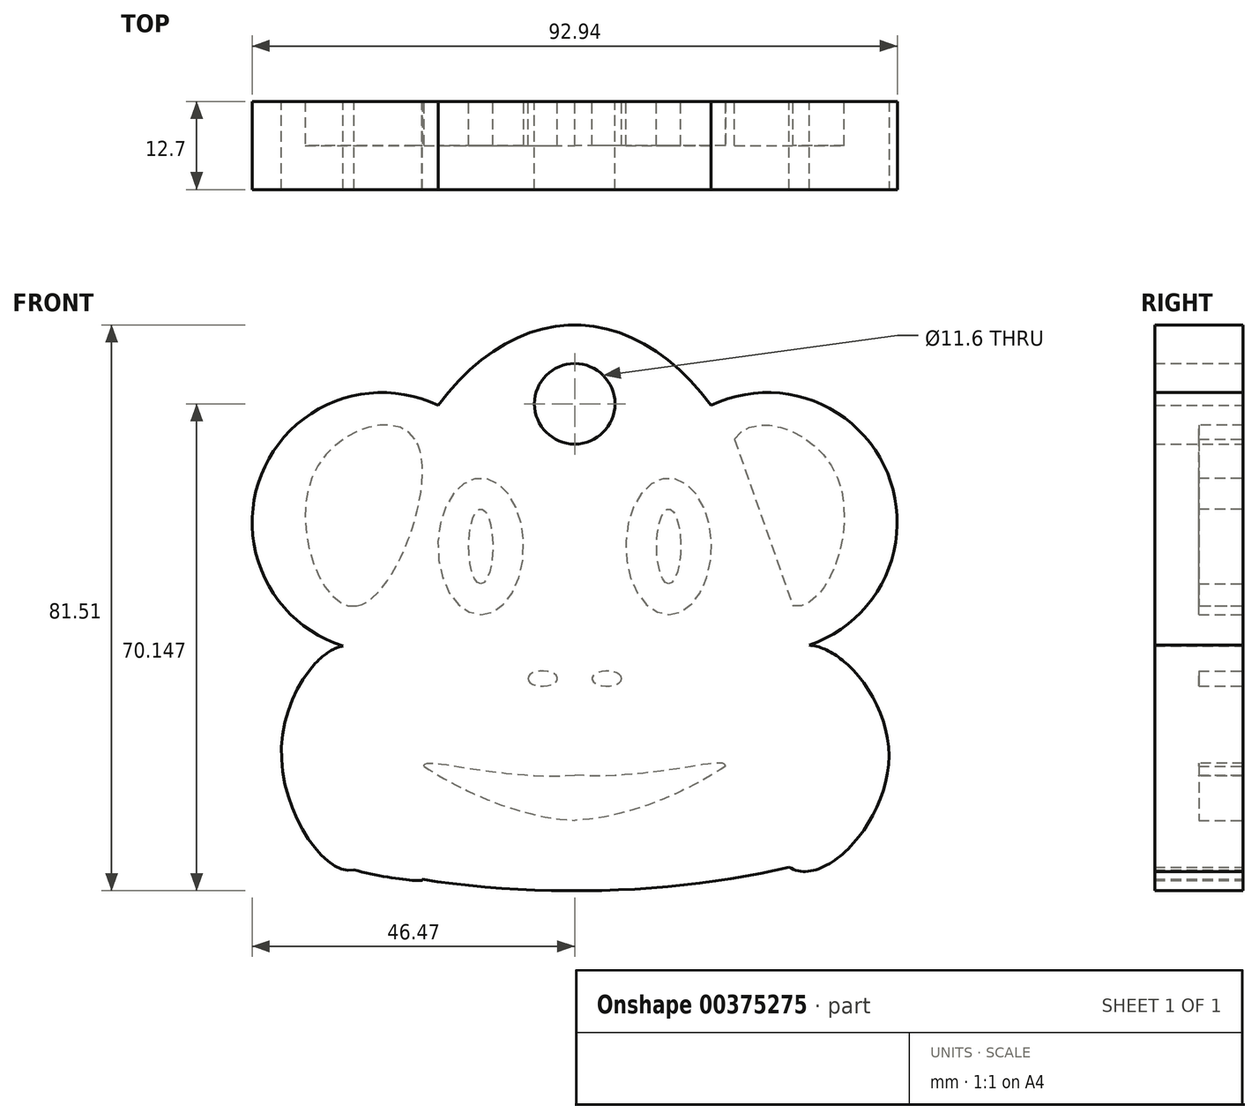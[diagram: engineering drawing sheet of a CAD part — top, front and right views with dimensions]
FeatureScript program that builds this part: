
annotation { "Feature Type Name" : "Feature", "Feature Type Description" : "" }
export const myFeature = defineFeature(function(context is Context, id is Id, definition is map)
    precondition{}
    {
        {
            var Q0;
            Q0=qCreatedBy(makeId("Front.planeOp"),FACE);
            var sketch = newSketch(context, id + "F0", { "sketchPlane" : qUnion([Q0])});
            skEllipticalArc(sketch, "E0", {});
            skEllipticalArc(sketch, "E1.trimOffspring", {});
            skFitSpline(sketch, "E2", {"points": [v(30.87, 4.09) * mm, v(45.27, -10.86) * mm, v(30.87, -27.14) * mm, v(30.87, 4.09) * mm]});
            skFitSpline(sketch, "E3", {"points": [v(-30.87, 4.09) * mm, v(-42.26, -10.19) * mm, v(-30.87, -27.14) * mm, v(-30.87, 4.09) * mm]});
            skFitSpline(sketch, "E4", {"points": [v(-31.81, -27.56) * mm, v(-22.04, -28.9) * mm, v(-35.7, -25.8) * mm, v(-31.81, -27.56) * mm]});
            skEllipticalArc(sketch, "E5.trimOffspring", {});
            skArc(sketch, "E6", {"start": v(30.87, 4.09) * mm, "mid": v(45.6, 28.18) * mm, "end": v(19.67, 39.36) * mm});
            skArc(sketch, "E7.MirrorCS", {"start": v(-30.87, 4.09) * mm, "mid": v(-45.6, 28.18) * mm, "end": v(-19.67, 39.36) * mm});
            const initialGuessF0  = {"E0": [0, -0.011525449343025684, 1, 0, 0.05395246669650078, 0.019038936975822335, 0.7315172091859318, 2.3355220649563564], "E1.trimOffspring": [0, 0, 0, -1, 0.05094582214951515, 0.030971134876745663, 1.6511394290076105, 4.632045878171976], "E5.trimOffspring": [0, -0.011525449343025684, 1, 0, 0.05395246669650078, 0.019038936975822335, 4.291597278907764, 5.530182504988913]};
            skSetInitialGuess(sketch, initialGuessF0);
            skSolve(sketch);
        }
        {
            var Q0;
            Q0 = qSketchRegion(id + "F0", true);
            var Q1;
            Q1=makeQuery(id+"F0.imprint","IMPRINT",FACE,{"disambiguationData":[TD([[makeQuery(id+"F0.imprint","IMPRINT",EDGE,{"derivedFrom":sQuery(id+"F0.wireOp",EDGE,"N9gW1YoA-lJsq-VaIs-6pUk-SrDH26mkGdG9")}),1.0]])]});
            var Q2;
            Q2=makeQuery(id+"F0.imprint","IMPRINT",FACE,{"disambiguationData":[TD([[makeQuery(id+"F0.imprint","IMPRINT",EDGE,{"derivedFrom":sQuery(id+"F0.wireOp",EDGE,"6f62b861-03d2-40b1-98b3-1ed908a5bce90.MirrorC")}),1.0]])]});
            extrude(context, id + "F1", {"entities" : qUnion([Q0, Q1, Q2]), "depth" : 12.7 * mm});
        }
        {
            var Q0;
            Q0=qCreatedBy(makeId("Front.planeOp"),FACE);
            var sketch = newSketch(context, id + "F2", { "sketchPlane" : qUnion([Q0])});
            skFitSpline(sketch, "E8", {"points": [v(-23, 34.5) * mm, v(-37.75, 29.23) * mm, v(-31.43, 10.46) * mm, v(-23, 34.5) * mm]});
            skLineSegment(sketch, "E9", {"start": v(-23, 34.5) * mm, "end": v(-31.43, 10.46) * mm});
            skEllipse(sketch, "E10", {"center": v(-13.54, 19.06) * mm, "majorRadius": 9.82 * mm, "minorRadius": 6.18 * mm, "majorAxis": v(0, -1)});
            skFitSpline(sketch, "E11", {"points": [v(0, -13.93) * mm, v(-26, -8.66) * mm, v(0, -20.42) * mm, v(21.73, -12.52) * mm, v(0, -13.93) * mm]});
            skLineSegment(sketch, "E12.MirrorCS", {"start": v(23, 34.5) * mm, "end": v(31.43, 10.46) * mm});
            skFitSpline(sketch, "E13.MirrorCS", {"points": [v(23, 34.5) * mm, v(37.75, 29.23) * mm, v(31.43, 10.46) * mm, v(23, 34.5) * mm]});
            skEllipse(sketch, "E14.MirrorC", {"center": v(13.54, 19.06) * mm, "majorRadius": 9.82 * mm, "minorRadius": 6.18 * mm, "majorAxis": v(0, -1)});
            skFitSpline(sketch, "E15.MirrorCS", {"points": [v(0, -13.93) * mm, v(26, -8.66) * mm, v(0, -20.42) * mm, v(-21.73, -12.52) * mm, v(0, -13.93) * mm]});
            skEllipse(sketch, "E16", {"center": v(-4.62, 0) * mm, "majorRadius": 2.12 * mm, "minorRadius": 1.1 * mm, "majorAxis": v(-1, 0)});
            skEllipse(sketch, "E17.MirrorC", {"center": v(4.62, 0) * mm, "majorRadius": 2.12 * mm, "minorRadius": 1.1 * mm, "majorAxis": v(1, 0)});
            skSolve(sketch);
        }
        {
            var Q0;
            Q0=makeQuery(id+"F2.imprint","IMPRINT",FACE,{"disambiguationData":[TD([[makeQuery(id+"F2.imprint","IMPRINT",EDGE,{"derivedFrom":sQuery(id+"F2.wireOp",EDGE,"E8")}),1.0]])]});
            var Q1;
            Q1=makeQuery(id+"F2.imprint","IMPRINT",FACE,{"disambiguationData":[TD([[makeQuery(id+"F2.imprint","IMPRINT",EDGE,{"derivedFrom":sQuery(id+"F2.wireOp",EDGE,"E10")}),1.0]])]});
            var Q2;
            Q2=makeQuery(id+"F2.imprint","IMPRINT",FACE,{"disambiguationData":[TD([[makeQuery(id+"F2.imprint","IMPRINT",EDGE,{"derivedFrom":sQuery(id+"F2.wireOp",EDGE,"E14.MirrorC")}),1.0]])]});
            var Q3;
            Q3=makeQuery(id+"F2.imprint","IMPRINT",FACE,{"disambiguationData":[TD([[makeQuery(id+"F2.imprint","IMPRINT",EDGE,{"derivedFrom":sQuery(id+"F2.wireOp",EDGE,"E12.MirrorCS")}),1.0]])]});
            var Q4;
            Q4=makeQuery(id+"F2.imprint","IMPRINT",FACE,{"disambiguationData":[TD([[makeQuery(id+"F2.imprint","IMPRINT",EDGE,{"derivedFrom":sQuery(id+"F2.wireOp",EDGE,"E11")}),1.0]])]});
            var Q5;
            Q5=makeQuery(id+"F2.imprint","IMPRINT",FACE,{"disambiguationData":[TD([[makeQuery(id+"F2.imprint","IMPRINT",EDGE,{"derivedFrom":sQuery(id+"F2.wireOp",EDGE,"E17.MirrorC")}),1.0]])]});
            var Q6;
            Q6=makeQuery(id+"F2.imprint","IMPRINT",FACE,{"disambiguationData":[TD([[makeQuery(id+"F2.imprint","IMPRINT",EDGE,{"derivedFrom":sQuery(id+"F2.wireOp",EDGE,"E16")}),1.0]])]});
            extrude(context, id + "F3", {"entities" : qUnion([Q0, Q1, Q2, Q3, Q4, Q5, Q6]), "operationType" : NewBodyOperationType.REMOVE, "depth" : 6.35 * mm});
        }
        {
            var Q0;
            Q0=makeQuery(id+"F1.opExtrude","CAP_FACE",FACE,{"disambiguationData":[OSD([sQuery(id+"F0.wireOp",EDGE,"E0"),sQuery(id+"F0.wireOp",EDGE,"E1.trimOffspring"),sQuery(id+"F0.wireOp",EDGE,"E2"),sQuery(id+"F0.wireOp",EDGE,"E3"),sQuery(id+"F0.wireOp",EDGE,"E4"),sQuery(id+"F0.wireOp",EDGE,"E5.trimOffspring"),sQuery(id+"F0.wireOp",EDGE,"E6"),sQuery(id+"F0.wireOp",EDGE,"E7.MirrorCS")])],"isStart":true});
            var sketch = newSketch(context, id + "F4", { "sketchPlane" : qUnion([Q0])});
            skEllipse(sketch, "E18", {"center": v(-13.54, 19.06) * mm, "majorRadius": 5.4 * mm, "minorRadius": 1.74 * mm, "majorAxis": v(0, -1)});
            skEllipse(sketch, "E19.MirrorC", {"center": v(13.54, 19.06) * mm, "majorRadius": 5.4 * mm, "minorRadius": 1.74 * mm, "majorAxis": v(0, -1)});
            skSolve(sketch);
        }
        {
            var Q0;
            Q0 = qSketchRegion(id + "F4", true);
            extrude(context, id + "F5", {"entities" : qUnion([Q0]), "oppositeDirection" : true, "depth" : 6.35 * mm});
        }
        {
            var Q0;
            Q0=qCreatedBy(makeId("Front.planeOp"),FACE);
            var sketch = newSketch(context, id + "F6", { "sketchPlane" : qUnion([Q0])});
            skCircle(sketch, "E20", {"center": v(0, 39.59) * mm, "radius": 5.8 * mm});
            skSolve(sketch);
        }
        {
            var Q0;
            Q0 = qSketchRegion(id + "F6", true);
            extrude(context, id + "F7", {"entities" : qUnion([Q0]), "operationType" : NewBodyOperationType.REMOVE, "depth" : 12.7 * mm});
        }
    });
